# Revit family: PD2 EN types Sans hôte
name_source: partatom
category: Dispositifs d'éclairage
units: mm (PartAtom-declared; Revit-internal decimal feet)

## family parameters
Basée sur le plan de construction = Oui
Conserver l'orientation des annotations = Non
Cote de connecteur circulaire = Utiliser le diamètre
Couper avec des vides une fois chargée = Non
Partagée = Non
Point de calcul de pièce = Non
Toujours verticalement = Oui
Type d'élément = Normal

## types (11) — shared parameters
Classe = II
Code d'assemblage = D5010200
Fabricant = B.E.G.
Hauteur de montage max = 300 cm
IP = 20
Image du type = 360°.jpg
Marque = LUXOMAT
Mode de pose = Encastré
URL = http://www.luxomat.com
zero-valued in all types: Elévation par défaut

## per-type parameters (varying)
| type | Alimentation | Charge Cos ɸ =0.5 | Charge Cos ɸ =1 | Charge LED | Commentaires du type | Consommation | Modèle | Relais | Référence | Température ambiante | Type de Sortie |
| 01- PD2 EN Générique | 110-240 V AC |  |  |  | DET.PRES.360°/Ø10M ENCASTRE |  | PD2 EN |  |  | -25°C à +50°C |  |
| 02- PD2 M 1C EN réf 92555 | 110-240 V AC | 1150 VA | 2300 W | 300 W | DET.PRES.MAITRE.1 CONTACT.360°/Ø10M ENCASTRE | 0,47 W | PD2 M 1C EN | 10 A | 92555 | -25°C à +50°C | TOR |
| 05- PD2 S EN réf 92156 | 110-240 V AC | 0 | 0 | 0 | DET.PRES.ESCLAVE..360°/Ø10M ENCASTRE | 0,25 W | PD2 S EN | 10 A | 92156 | -25°C à +50°C | Esclave |
| 03- PD2 M 2C EN réf 92155 | 110-240 V AC | 1150 VA | 2300 W | 300 W | DET.PRES.MAITRE.2 CONTACTS.360°/Ø10M ENCASTRE | 0,52 W | PD2 M 2C EN | 10 A | 92155 | -25°C à +50°C | TOR |
| 04- PD2 M DIM EN réf 92157 | 110-240 V AC | 1150 VA | 2300 W | 300 W | DET.PRES.MAITRE.DIM(1-10V).360°/Ø10M ENCASTRE | 0,47 W | PD2 M DIM EN | 10 A | 92157 | -25°C à +50°C | DIM (50 ballasts maxi) |
| 10- PD2N KNX DX EN réf 93361 | 24 V DC par Bus KNX | 0 | 0 | 0 | DET.PRES.KNX.VERSION DELUXE.360°/Ø10M ENCASTRE | 12 mA | PD2N KNX DX EN | 0 | 93361 | -5°C à +45°C | KNX - 1 sortie Eclairage TOR ou GRADATION / 3 sorties Présence / Capteur de température et bruit |
| 08- PD2N KNX BA EN réf 93381 | 24 V DC par Bus KNX | 0 | 0 | 0 | DET.PRES.KNX.VERSION BASIQUE.360°/Ø10M ENCASTRE | 12 mA | PD2N KNX BA EN | 0 | 93381 | -5°C à +45°C | KNX - 1 sortie Eclairage TOR |
| 09- PD2N KNX ST EN réf 93383 | 24 V DC par Bus KNX | 0 | 0 | 0 | DET.PRES.KNX.VERSION STANDARD.360°/Ø10M ENCASTRE | 12 mA | PD2N KNX ST EN | 0 | 93383 | -5°C à +45°C | KNX - 1 sortie Eclairage TOR ou GRADATION / 3 sorties Présence |
| 07- PD2N BMS DALI 2 EN réf 93544 | 10-22 V DC par Bus DALI | 0 | 0 | 0 | MULTI.CAPTEUR.PRES.BMS-DALI 2.360°/Ø10M ENCASTRE | 7 mA | PD2N BMS DALI 2 EN | 0 | 93544 | -25°C à +55°C | DALI 2 Adressable - BMS |
| 11- PD2N KNXs ST EN réf 93511 | 24 V DC par Bus KNX | 0 | 0 | 0 | DET.PRES.KNX Sécure.VERSION STANDARD.360°/Ø10M ENCASTRE | 12 mA | PD2N KNXs ST EN | 0 | 93511 | -5°C à +45°C | KNX Sécure - 1 sortie Eclairage TOR ou GRADATION / 3 sorties Présence / HCL |
| 12- PD2N KNXs DX EN réf 93513 | 24 V DC par Bus KNX | 0 | 0 | 0 | DET.PRES.KNX Sécure.VERSION DELUXE.360°/Ø10M ENCASTRE | 12 mA | PD2N KNXs DX EN | 0 | 93513 | -5°C à +45°C | KNX Sécure - 1 sortie Eclairage TOR ou GRADATION / 3 sorties Présence / Capteur de température et bruit / HCL |
